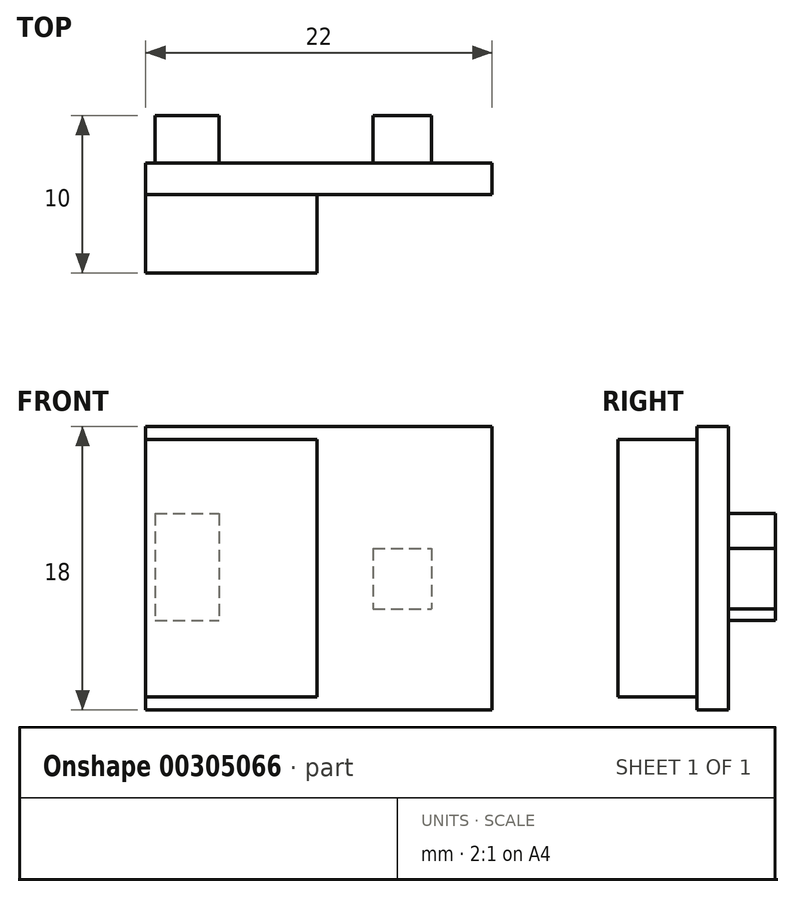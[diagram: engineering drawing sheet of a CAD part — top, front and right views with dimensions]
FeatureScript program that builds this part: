
annotation { "Feature Type Name" : "Feature", "Feature Type Description" : "" }
export const myFeature = defineFeature(function(context is Context, id is Id, definition is map)
    precondition{}
    {
        {
            var Q0;
            Q0=qCreatedBy(makeId("Front.planeOp"),FACE);
            var sketch = newSketch(context, id + "F0", { "sketchPlane" : qUnion([Q0])});
            skLineSegment(sketch, "E0.bottom", {"start": v(-41.86, -13.06) * mm, "end": v(-19.86, -13.06) * mm});
            skLineSegment(sketch, "E0.top", {"start": v(-41.86, -31.06) * mm, "end": v(-19.86, -31.06) * mm});
            skLineSegment(sketch, "E0.left", {"start": v(-41.86, -13.06) * mm, "end": v(-41.86, -31.06) * mm});
            skLineSegment(sketch, "E0.right", {"start": v(-19.86, -13.06) * mm, "end": v(-19.86, -31.06) * mm});
            skLineSegment(sketch, "E1.bottom", {"start": v(-30.98, -13.89) * mm, "end": v(-41.86, -13.89) * mm});
            skLineSegment(sketch, "E1.top", {"start": v(-30.98, -30.24) * mm, "end": v(-41.86, -30.24) * mm});
            skLineSegment(sketch, "E1.left", {"start": v(-30.98, -13.89) * mm, "end": v(-30.98, -30.24) * mm});
            skLineSegment(sketch, "E1.right", {"start": v(-41.86, -13.89) * mm, "end": v(-41.86, -30.24) * mm});
            skLineSegment(sketch, "E2", {"start": v(-41.86, -22.06) * mm, "end": v(-19.86, -22.06) * mm, "construction": true});
            skPoint(sketch, "E3", {"position": v(-41.86, -22.06) * mm});
            skSolve(sketch);
        }
        {
            var Q0;
            Q0 = qSketchRegion(id + "F0", true);
            extrude(context, id + "F1", {"entities" : qUnion([Q0]), "depth" : 2 * mm});
        }
        {
            var Q0;
            Q0=makeQuery(id+"F0.imprint","IMPRINT",FACE,{"disambiguationData":[TD([[makeQuery(id+"F0.imprint","IMPRINT",EDGE,{"derivedFrom":sQuery(id+"F0.wireOp",EDGE,"E1.bottom")}),1.0]])]});
            extrude(context, id + "F2", {"entities" : qUnion([Q0]), "operationType" : NewBodyOperationType.ADD, "depth" : 7 * mm});
        }
        {
            var Q0;
            Q0=makeQuery(id+"F1.opExtrude","CAP_FACE",FACE,{"disambiguationData":[OSD([sQuery(id+"F0.wireOp",EDGE,"E0.bottom"),sQuery(id+"F0.wireOp",EDGE,"E0.top"),sQuery(id+"F0.wireOp",EDGE,"E0.left"),sQuery(id+"F0.wireOp",EDGE,"E0.right"),sQuery(id+"F0.wireOp",EDGE,"E1.right")])],"isStart":true});
            var sketch = newSketch(context, id + "F3", { "sketchPlane" : qUnion([Q0])});
            skLineSegment(sketch, "E4.bottom", {"start": v(41.26, -18.59) * mm, "end": v(37.2, -18.59) * mm});
            skLineSegment(sketch, "E4.top", {"start": v(41.26, -25.38) * mm, "end": v(37.2, -25.38) * mm});
            skLineSegment(sketch, "E4.left", {"start": v(41.26, -18.59) * mm, "end": v(41.26, -25.38) * mm});
            skLineSegment(sketch, "E4.right", {"start": v(37.2, -18.59) * mm, "end": v(37.2, -25.38) * mm});
            skLineSegment(sketch, "E5.bottom", {"start": v(27.42, -20.8) * mm, "end": v(23.72, -20.8) * mm});
            skLineSegment(sketch, "E5.top", {"start": v(27.42, -24.65) * mm, "end": v(23.72, -24.65) * mm});
            skLineSegment(sketch, "E5.left", {"start": v(27.42, -20.8) * mm, "end": v(27.42, -24.65) * mm});
            skLineSegment(sketch, "E5.right", {"start": v(23.72, -20.8) * mm, "end": v(23.72, -24.65) * mm});
            skSolve(sketch);
        }
        {
            var Q0;
            Q0 = qSketchRegion(id + "F3", true);
            extrude(context, id + "F4", {"entities" : qUnion([Q0]), "operationType" : NewBodyOperationType.ADD, "depth" : 3 * mm});
        }
    });
